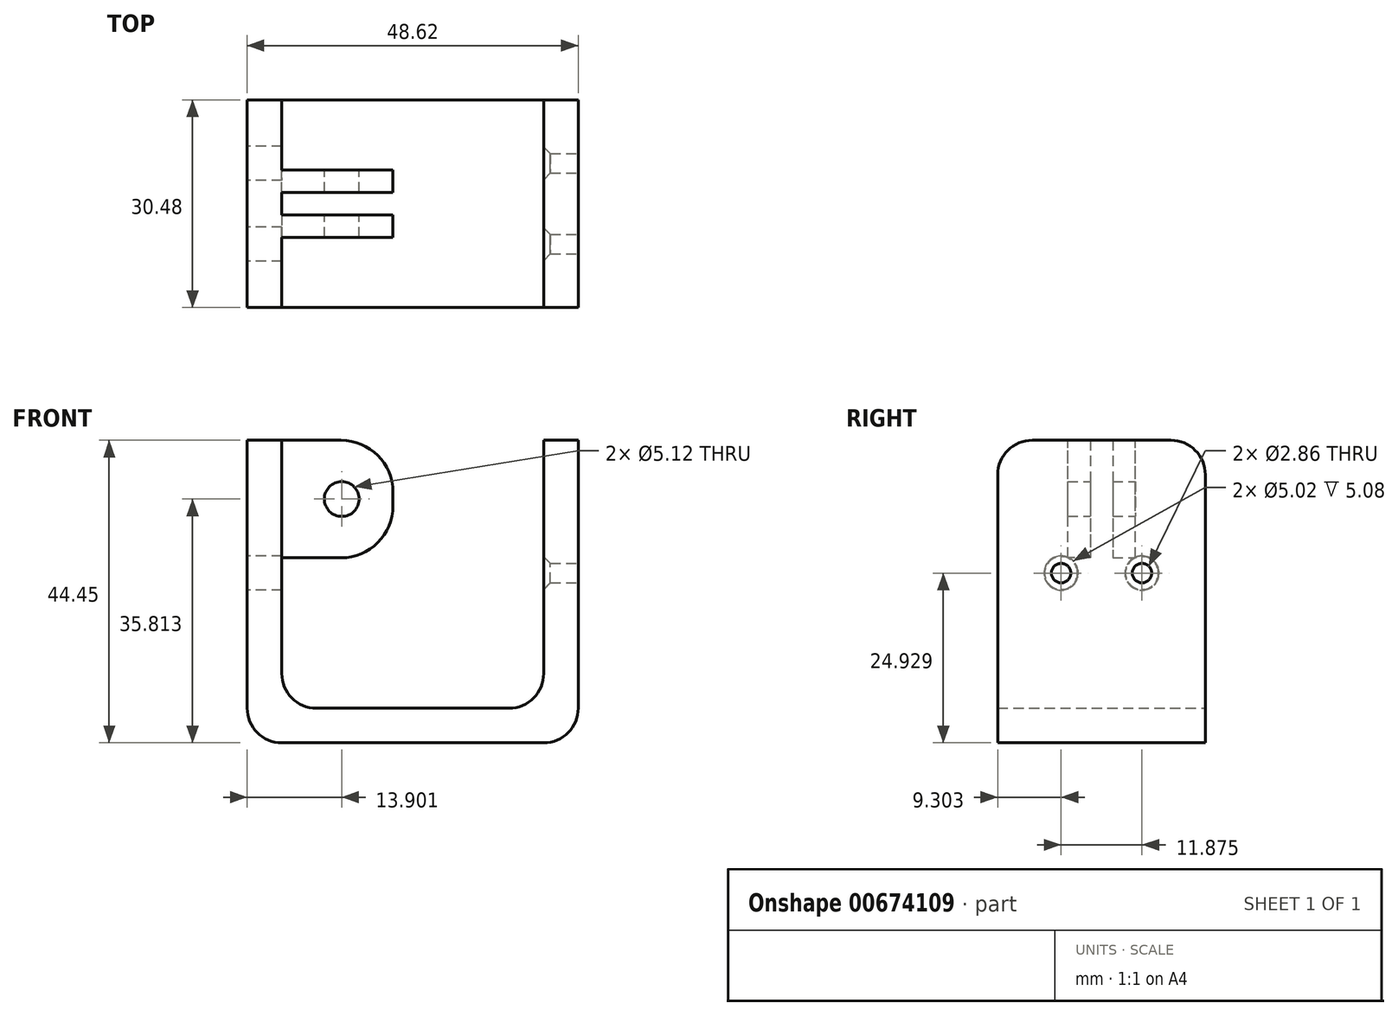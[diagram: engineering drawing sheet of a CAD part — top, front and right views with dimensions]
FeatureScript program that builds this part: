
annotation { "Feature Type Name" : "Feature", "Feature Type Description" : "" }
export const myFeature = defineFeature(function(context is Context, id is Id, definition is map)
    precondition{}
    {
        {
            var Q0;
            Q0=qCreatedBy(makeId("Front.planeOp"),FACE);
            var sketch = newSketch(context, id + "F0", { "sketchPlane" : qUnion([Q0])});
            skLineSegment(sketch, "E0", {"start": v(-25.3, 29.09) * mm, "end": v(-25.3, -15.36) * mm});
            skLineSegment(sketch, "E1", {"start": v(-25.3, -15.36) * mm, "end": v(23.31, -15.36) * mm});
            skLineSegment(sketch, "E2", {"start": v(23.31, -15.36) * mm, "end": v(23.31, 29.09) * mm});
            skLineSegment(sketch, "E3", {"start": v(23.31, 29.09) * mm, "end": v(18.23, 29.09) * mm});
            skLineSegment(sketch, "E4", {"start": v(18.23, 29.09) * mm, "end": v(18.23, -10.28) * mm});
            skLineSegment(sketch, "E5", {"start": v(18.23, -10.28) * mm, "end": v(-20.23, -10.28) * mm});
            skLineSegment(sketch, "E6", {"start": v(-20.23, -10.28) * mm, "end": v(-20.23, 29.09) * mm});
            skLineSegment(sketch, "E7", {"start": v(-20.23, 29.09) * mm, "end": v(-25.3, 29.09) * mm});
            skSolve(sketch);
        }
        {
            var Q0;
            Q0=makeQuery(id+"F0.imprint","IMPRINT",FACE,{"disambiguationData":[TD([[makeQuery(id+"F0.imprint","IMPRINT",EDGE,{"derivedFrom":sQuery(id+"F0.wireOp",EDGE,"E0")}),1.0]])]});
            extrude(context, id + "F1", {"entities" : qUnion([Q0]), "depth" : 30.48 * mm, "offsetDistance" : 25.4 * mm});
        }
        {
            var Q0;
            Q0=makeQuery(id+"F1.opExtrude","SWEPT_FACE",FACE,{"disambiguationData":[OSD([sQuery(id+"F0.wireOp",EDGE,"E2")])]});
            var sketch = newSketch(context, id + "F2", { "sketchPlane" : qUnion([Q0])});
            skLineSegment(sketch, "E8", {"start": v(-15.24, 29.09) * mm, "end": v(-15.24, 9.57) * mm});
            skPoint(sketch, "E8.endSnap0", {"position": v(-15.24, 29.09) * mm});
            skLineSegment(sketch, "E9", {"start": v(-15.24, 9.57) * mm, "end": v(-21.18, 9.57) * mm});
            skLineSegment(sketch, "E10", {"start": v(-21.18, 9.57) * mm, "end": v(-15.24, 9.57) * mm});
            skLineSegment(sketch, "E11", {"start": v(-9.3, 9.57) * mm, "end": v(-15.24, 9.57) * mm});
            skCircle(sketch, "E12", {"center": v(-21.18, 9.57) * mm, "radius": 1.43 * mm});
            skCircle(sketch, "E13", {"center": v(-9.3, 9.57) * mm, "radius": 1.43 * mm});
            skLineSegment(sketch, "E14", {"start": v(-15.24, 9.57) * mm, "end": v(-15.24, 3.63) * mm});
            skLineSegment(sketch, "E15", {"start": v(-15.24, 3.63) * mm, "end": v(-15.24, 9.57) * mm});
            skLineSegment(sketch, "E16", {"start": v(-15.24, 9.57) * mm, "end": v(-15.24, 15.51) * mm});
            skSolve(sketch);
        }
        {
            var Q0;
            Q0 = qSketchRegion(id + "F2", true);
            extrude(context, id + "F3", {"entities" : qUnion([Q0]), "operationType" : NewBodyOperationType.REMOVE, "oppositeDirection" : true, "depth" : 67.94 * mm, "offsetDistance" : 25.4 * mm});
        }
        {
            var Q0;
            Q0=makeQuery(id+"F1.opExtrude","CAP_EDGE",EDGE,{"disambiguationData":[OSD([sQuery(id+"F0.wireOp",EDGE,"E3")])],"isStart":true});
            var Q1;
            Q1=makeQuery(id+"F1.opExtrude","CAP_EDGE",EDGE,{"disambiguationData":[OSD([sQuery(id+"F0.wireOp",EDGE,"E3")])],"isStart":false});
            fillet(context, id + "F4", {"entities" : qUnion([Q0, Q1]), "radius" : 5.08 * mm, "tangentPropagation" : true, "allowEdgeOverflow" : false});
        }
        {
            var Q0;
            Q0=makeQuery(id+"F1.opExtrude","SWEPT_EDGE",EDGE,{"disambiguationData":[OSD([sQuery(id+"F0.wireOp",EDGE,"E1"),sQuery(id+"F0.wireOp",EDGE,"E2")])]});
            var Q1;
            Q1=makeQuery(id+"F1.opExtrude","SWEPT_EDGE",EDGE,{"disambiguationData":[OSD([sQuery(id+"F0.wireOp",EDGE,"E4"),sQuery(id+"F0.wireOp",EDGE,"E5")])]});
            fillet(context, id + "F5", {"entities" : qUnion([Q0, Q1]), "radius" : 5.08 * mm, "tangentPropagation" : true, "allowEdgeOverflow" : false});
        }
        {
            var Q0;
            Q0=makeQuery(id+"F1.opExtrude","SWEPT_EDGE",EDGE,{"disambiguationData":[OSD([sQuery(id+"F0.wireOp",EDGE,"E5"),sQuery(id+"F0.wireOp",EDGE,"E6")])]});
            var Q1;
            Q1=makeQuery(id+"F1.opExtrude","SWEPT_EDGE",EDGE,{"disambiguationData":[OSD([sQuery(id+"F0.wireOp",EDGE,"E0"),sQuery(id+"F0.wireOp",EDGE,"E1")])]});
            fillet(context, id + "F6", {"entities" : qUnion([Q0, Q1]), "radius" : 5.08 * mm, "tangentPropagation" : true, "allowEdgeOverflow" : false});
        }
        {
            var Q0;
            Q0=makeQuery(id+"F3.boolean.opBoolean","INTERSECT",EDGE,{"derivedFrom":[makeQuery(id+"F1.opExtrude","SWEPT_FACE",FACE,{"disambiguationData":[OSD([sQuery(id+"F0.wireOp",EDGE,"E4")])]}),makeQuery(id+"F3.opExtrude","SWEPT_FACE",FACE,{"disambiguationData":[OSD([sQuery(id+"F2.wireOp",EDGE,"kRmBFZ00-me5Y-tS20-5NTX-MWHyAIRY3x5K")])]})]});
            var Q1;
            Q1=makeQuery(id+"F3.boolean.opBoolean","INTERSECT",EDGE,{"derivedFrom":[makeQuery(id+"F1.opExtrude","SWEPT_FACE",FACE,{"disambiguationData":[OSD([sQuery(id+"F0.wireOp",EDGE,"E4")])]}),makeQuery(id+"F3.opExtrude","SWEPT_FACE",FACE,{"disambiguationData":[OSD([sQuery(id+"F2.wireOp",EDGE,"E13")])]})]});
            var Q2;
            Q2=makeQuery(id+"F3.boolean.opBoolean","INTERSECT",EDGE,{"derivedFrom":[makeQuery(id+"F1.opExtrude","SWEPT_FACE",FACE,{"disambiguationData":[OSD([sQuery(id+"F0.wireOp",EDGE,"E4")])]}),makeQuery(id+"F3.opExtrude","SWEPT_FACE",FACE,{"disambiguationData":[OSD([sQuery(id+"F2.wireOp",EDGE,"E12")])]})]});
            var Q3;
            Q3=makeQuery(id+"F3.boolean.opBoolean","INTERSECT",EDGE,{"derivedFrom":[makeQuery(id+"F1.opExtrude","SWEPT_FACE",FACE,{"disambiguationData":[OSD([sQuery(id+"F0.wireOp",EDGE,"E4")])]}),makeQuery(id+"F3.opExtrude","SWEPT_FACE",FACE,{"disambiguationData":[OSD([sQuery(id+"F2.wireOp",EDGE,"bg4zosgj-CZyq-8HZh-7LQW-iAubO1l1dHWn")])]})]});
            chamfer(context, id + "F7", {"entities" : qUnion([Q0, Q1, Q2, Q3]), "width" : 0.99 * mm, "tangentPropagation" : true});
        }
        {
            var Q0;
            Q0=makeQuery(id+"F1.opExtrude","SWEPT_FACE",FACE,{"disambiguationData":[OSD([sQuery(id+"F0.wireOp",EDGE,"E0")])]});
            var sketch = newSketch(context, id + "F8", { "sketchPlane" : qUnion([Q0])});
            skCircle(sketch, "E17", {"center": v(21.18, 9.57) * mm, "radius": 2.5 * mm});
            skCircle(sketch, "E18", {"center": v(9.3, 9.57) * mm, "radius": 2.5 * mm});
            skSolve(sketch);
        }
        {
            var Q0;
            Q0 = qSketchRegion(id + "F8", true);
            extrude(context, id + "F9", {"entities" : qUnion([Q0]), "operationType" : NewBodyOperationType.REMOVE, "oppositeDirection" : true, "depth" : 18.16 * mm, "offsetDistance" : 25.4 * mm});
        }
        {
            var Q0;
            Q0=makeQuery(id+"F1.opExtrude","SWEPT_FACE",FACE,{"disambiguationData":[OSD([sQuery(id+"F0.wireOp",EDGE,"E6")])]});
            var sketch = newSketch(context, id + "F10", { "sketchPlane" : qUnion([Q0])});
            skLineSegment(sketch, "E19", {"start": v(-16.9, 29.09) * mm, "end": v(-13.59, 29.09) * mm});
            skLineSegment(sketch, "E20", {"start": v(-13.59, 29.09) * mm, "end": v(-13.59, 11.82) * mm});
            skLineSegment(sketch, "E21", {"start": v(-13.59, 11.82) * mm, "end": v(-10.29, 11.82) * mm});
            skLineSegment(sketch, "E22", {"start": v(-10.29, 11.82) * mm, "end": v(-10.29, 29.09) * mm});
            skLineSegment(sketch, "E23", {"start": v(-10.29, 29.09) * mm, "end": v(-13.59, 29.09) * mm});
            skLineSegment(sketch, "E24", {"start": v(-16.9, 29.09) * mm, "end": v(-16.9, 11.82) * mm});
            skLineSegment(sketch, "E25", {"start": v(-16.9, 11.82) * mm, "end": v(-20.2, 11.82) * mm});
            skLineSegment(sketch, "E26", {"start": v(-20.2, 11.82) * mm, "end": v(-20.2, 29.09) * mm});
            skLineSegment(sketch, "E27", {"start": v(-20.2, 29.09) * mm, "end": v(-16.9, 29.09) * mm});
            skSolve(sketch);
        }
        {
            var Q0;
            Q0 = qSketchRegion(id + "F10", true);
            extrude(context, id + "F11", {"entities" : qUnion([Q0]), "operationType" : NewBodyOperationType.ADD, "depth" : 16.33 * mm, "offsetDistance" : 25.4 * mm});
        }
        {
            var Q0;
            Q0=makeQuery(id+"F1.opExtrude","CAP_EDGE",EDGE,{"disambiguationData":[OSD([sQuery(id+"F0.wireOp",EDGE,"E7")])],"isStart":true});
            var Q1;
            Q1=makeQuery(id+"F1.opExtrude","CAP_EDGE",EDGE,{"disambiguationData":[OSD([sQuery(id+"F0.wireOp",EDGE,"E7")])],"isStart":false});
            fillet(context, id + "F12", {"entities" : qUnion([Q0, Q1]), "radius" : 5.08 * mm, "tangentPropagation" : true, "allowEdgeOverflow" : false});
        }
        {
            var Q0;
            Q0=makeQuery(id+"F11.opExtrude","CAP_EDGE",EDGE,{"disambiguationData":[OSD([sQuery(id+"F10.wireOp",EDGE,"E23")])],"isStart":false});
            var Q1;
            Q1=makeQuery(id+"F11.opExtrude","CAP_EDGE",EDGE,{"disambiguationData":[OSD([sQuery(id+"F10.wireOp",EDGE,"E21")])],"isStart":false});
            fillet(context, id + "F13", {"entities" : qUnion([Q0, Q1]), "radius" : 7.62 * mm, "tangentPropagation" : true, "allowEdgeOverflow" : false});
        }
        {
            var Q0;
            Q0=makeQuery(id+"F11.opExtrude","CAP_EDGE",EDGE,{"disambiguationData":[OSD([sQuery(id+"F10.wireOp",EDGE,"E27")])],"isStart":false});
            var Q1;
            Q1=makeQuery(id+"F11.opExtrude","CAP_EDGE",EDGE,{"disambiguationData":[OSD([sQuery(id+"F10.wireOp",EDGE,"E25")])],"isStart":false});
            fillet(context, id + "F14", {"entities" : qUnion([Q0, Q1]), "radius" : 7.62 * mm, "tangentPropagation" : true, "allowEdgeOverflow" : false});
        }
        {
            var Q0;
            Q0=makeQuery(id+"F11.opExtrude","SWEPT_FACE",FACE,{"disambiguationData":[OSD([sQuery(id+"F10.wireOp",EDGE,"E22")])]});
            var sketch = newSketch(context, id + "F15", { "sketchPlane" : qUnion([Q0])});
            skLineSegment(sketch, "E28", {"start": v(3.9, 20.45) * mm, "end": v(11.4, 20.45) * mm});
            skCircle(sketch, "E29", {"center": v(11.4, 20.45) * mm, "radius": 2.56 * mm});
            skSolve(sketch);
        }
        {
            var Q0;
            Q0 = qSketchRegion(id + "F15", true);
            extrude(context, id + "F16", {"entities" : qUnion([Q0]), "operationType" : NewBodyOperationType.REMOVE, "oppositeDirection" : true, "depth" : 25.4 * mm, "offsetDistance" : 25.4 * mm});
        }
    });
